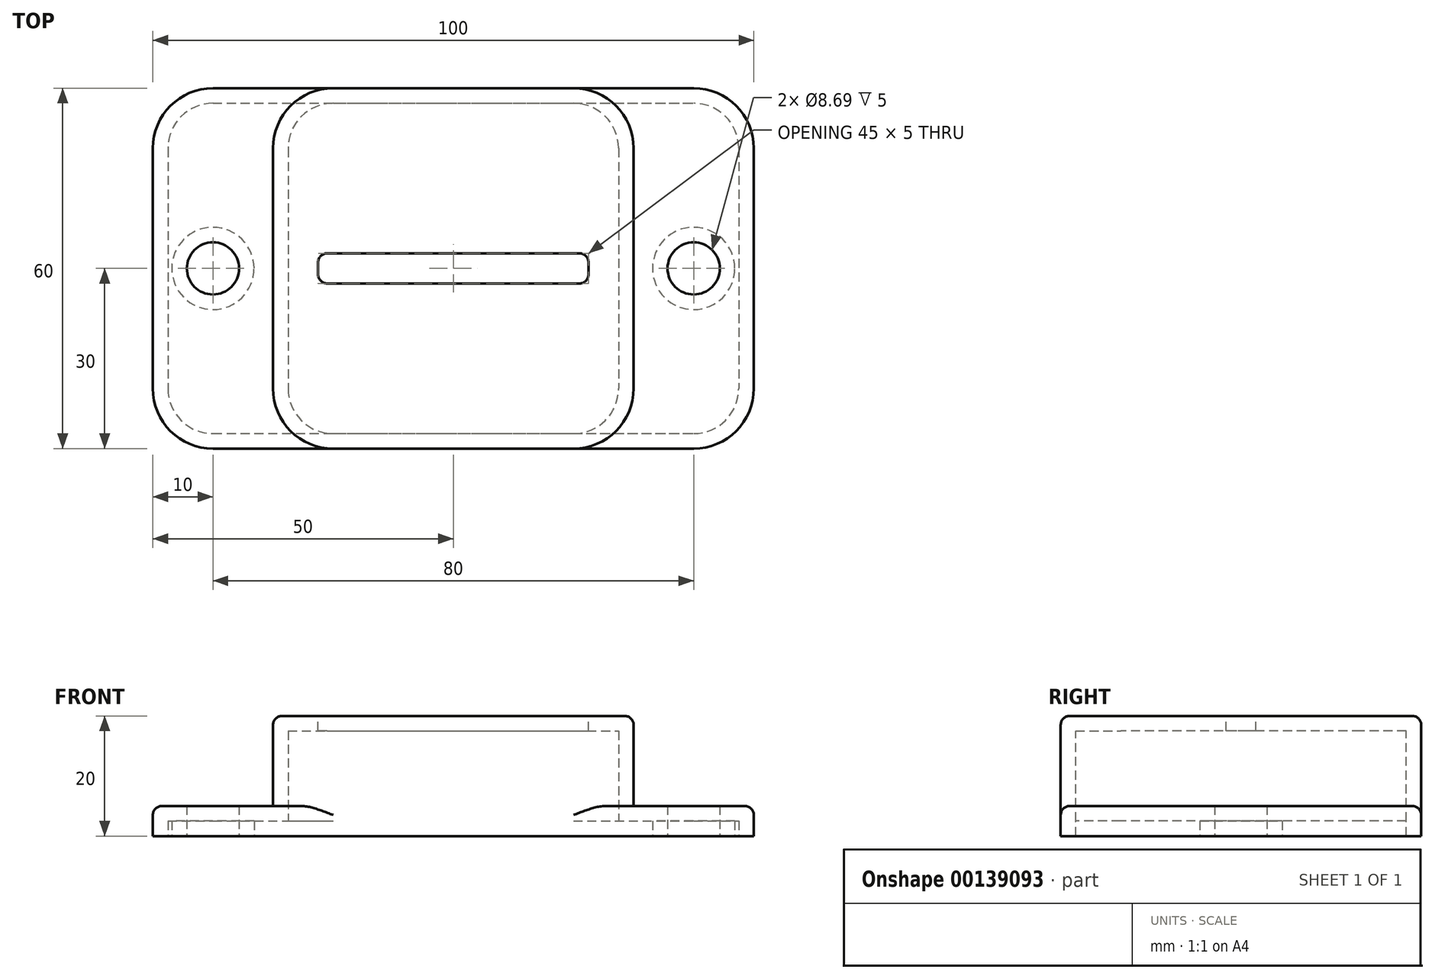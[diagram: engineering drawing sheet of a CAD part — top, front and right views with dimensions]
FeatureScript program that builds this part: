
annotation { "Feature Type Name" : "Feature", "Feature Type Description" : "" }
export const myFeature = defineFeature(function(context is Context, id is Id, definition is map)
    precondition{}
    {
        {
            var Q0;
            Q0=qCreatedBy(makeId("Top.planeOp"),FACE);
            var sketch = newSketch(context, id + "F0", { "sketchPlane" : qUnion([Q0])});
            skLineSegment(sketch, "E0.bottom", {"start": v(-40, 30) * mm, "end": v(40, 30) * mm});
            skLineSegment(sketch, "E0.top", {"start": v(-40, -30) * mm, "end": v(40, -30) * mm});
            skLineSegment(sketch, "E0.left", {"start": v(-50, 20) * mm, "end": v(-50, -20) * mm});
            skLineSegment(sketch, "E0.right", {"start": v(50, 20) * mm, "end": v(50, -20) * mm});
            skPoint(sketch, "E1.visualSharp", {"position": v(-50, -30) * mm});
            skArc(sketch, "E1.filletArc", {"start": v(-50, -20) * mm, "mid": v(-47.07, -27.07) * mm, "end": v(-40, -30) * mm});
            skPoint(sketch, "E2.visualSharp", {"position": v(-50, 30) * mm});
            skArc(sketch, "E2.filletArc", {"start": v(-40, 30) * mm, "mid": v(-47.07, 27.07) * mm, "end": v(-50, 20) * mm});
            skPoint(sketch, "E3.visualSharp", {"position": v(50, 30) * mm});
            skArc(sketch, "E3.filletArc", {"start": v(50, 20) * mm, "mid": v(47.07, 27.07) * mm, "end": v(40, 30) * mm});
            skPoint(sketch, "E4.visualSharp", {"position": v(50, -30) * mm});
            skArc(sketch, "E4.filletArc", {"start": v(40, -30) * mm, "mid": v(47.07, -27.07) * mm, "end": v(50, -20) * mm});
            skCircle(sketch, "E5", {"center": v(-40, 0) * mm, "radius": 4.34 * mm});
            skCircle(sketch, "E6", {"center": v(40, 0) * mm, "radius": 4.34 * mm});
            skSolve(sketch);
        }
        {
            var Q0;
            Q0=makeQuery(id+"F0.imprint","IMPRINT",FACE,{"disambiguationData":[TD([[makeQuery(id+"F0.imprint","IMPRINT",EDGE,{"derivedFrom":sQuery(id+"F0.wireOp",EDGE,"E0.bottom")}),-1.0]])]});
            extrude(context, id + "F1", {"entities" : qUnion([Q0]), "depth" : 5 * mm});
        }
        {
            var Q0;
            Q0=makeQuery(id+"F1.opExtrude","CAP_FACE",FACE,{"disambiguationData":[OSD([sQuery(id+"F0.wireOp",EDGE,"E0.bottom"),sQuery(id+"F0.wireOp",EDGE,"E0.top"),sQuery(id+"F0.wireOp",EDGE,"E0.left"),sQuery(id+"F0.wireOp",EDGE,"E0.right"),sQuery(id+"F0.wireOp",EDGE,"E1.filletArc"),sQuery(id+"F0.wireOp",EDGE,"E2.filletArc"),sQuery(id+"F0.wireOp",EDGE,"E3.filletArc"),sQuery(id+"F0.wireOp",EDGE,"E4.filletArc"),sQuery(id+"F0.wireOp",EDGE,"E5"),sQuery(id+"F0.wireOp",EDGE,"E6")])],"isStart":false});
            var sketch = newSketch(context, id + "F2", { "sketchPlane" : qUnion([Q0])});
            skLineSegment(sketch, "E7.bottom", {"start": v(-20, 30) * mm, "end": v(20, 30) * mm});
            skLineSegment(sketch, "E7.top", {"start": v(-20, -30) * mm, "end": v(20, -30) * mm});
            skLineSegment(sketch, "E7.left", {"start": v(-30, 20) * mm, "end": v(-30, -20) * mm});
            skLineSegment(sketch, "E7.right", {"start": v(30, 20) * mm, "end": v(30, -20) * mm});
            skPoint(sketch, "E8.visualSharp", {"position": v(-30, 30) * mm});
            skArc(sketch, "E8.filletArc", {"start": v(-20, 30) * mm, "mid": v(-27.07, 27.07) * mm, "end": v(-30, 20) * mm});
            skPoint(sketch, "E9.visualSharp", {"position": v(30, 30) * mm});
            skArc(sketch, "E9.filletArc", {"start": v(30, 20) * mm, "mid": v(27.07, 27.07) * mm, "end": v(20, 30) * mm});
            skPoint(sketch, "E10.visualSharp", {"position": v(30, -30) * mm});
            skArc(sketch, "E10.filletArc", {"start": v(20, -30) * mm, "mid": v(27.07, -27.07) * mm, "end": v(30, -20) * mm});
            skPoint(sketch, "E11.visualSharp", {"position": v(-30, -30) * mm});
            skArc(sketch, "E11.filletArc", {"start": v(-30, -20) * mm, "mid": v(-27.07, -27.07) * mm, "end": v(-20, -30) * mm});
            skSolve(sketch);
        }
        {
            var Q0;
            Q0=makeQuery(id+"F2.imprint","IMPRINT",FACE,{"disambiguationData":[TD([[makeQuery(id+"F2.imprint","IMPRINT",EDGE,{"derivedFrom":sQuery(id+"F2.wireOp",EDGE,"E7.bottom")}),-1.0]])]});
            extrude(context, id + "F3", {"entities" : qUnion([Q0]), "operationType" : NewBodyOperationType.ADD, "depth" : 15 * mm});
        }
        {
            var Q0;
            Q0=makeQuery(id+"F1.opExtrude","CAP_FACE",FACE,{"disambiguationData":[OSD([sQuery(id+"F0.wireOp",EDGE,"E0.bottom"),sQuery(id+"F0.wireOp",EDGE,"E0.top"),sQuery(id+"F0.wireOp",EDGE,"E0.left"),sQuery(id+"F0.wireOp",EDGE,"E0.right"),sQuery(id+"F0.wireOp",EDGE,"E1.filletArc"),sQuery(id+"F0.wireOp",EDGE,"E2.filletArc"),sQuery(id+"F0.wireOp",EDGE,"E3.filletArc"),sQuery(id+"F0.wireOp",EDGE,"E4.filletArc"),sQuery(id+"F0.wireOp",EDGE,"E5"),sQuery(id+"F0.wireOp",EDGE,"E6")])],"isStart":true});
            shell(context, id + "F4", {"entities" : qUnion([Q0]), "thickness" : 2.5 * mm});
        }
        {
            var Q0;
            Q0=makeQuery(id+"F3.opExtrude","CAP_FACE",FACE,{"disambiguationData":[OSD([sQuery(id+"F2.wireOp",EDGE,"E7.bottom"),sQuery(id+"F2.wireOp",EDGE,"E7.top"),sQuery(id+"F2.wireOp",EDGE,"E7.left"),sQuery(id+"F2.wireOp",EDGE,"E7.right"),sQuery(id+"F2.wireOp",EDGE,"E8.filletArc"),sQuery(id+"F2.wireOp",EDGE,"E9.filletArc"),sQuery(id+"F2.wireOp",EDGE,"E10.filletArc"),sQuery(id+"F2.wireOp",EDGE,"E11.filletArc")])],"isStart":false});
            var sketch = newSketch(context, id + "F5", { "sketchPlane" : qUnion([Q0])});
            skLineSegment(sketch, "E12.bottom", {"start": v(-22.5, 2.5) * mm, "end": v(22.5, 2.5) * mm});
            skLineSegment(sketch, "E12.top", {"start": v(-22.5, -2.5) * mm, "end": v(22.5, -2.5) * mm});
            skLineSegment(sketch, "E12.left", {"start": v(-22.5, 2.5) * mm, "end": v(-22.5, -2.5) * mm});
            skLineSegment(sketch, "E12.right", {"start": v(22.5, 2.5) * mm, "end": v(22.5, -2.5) * mm});
            skPoint(sketch, "E12.middle", {"position": v(0, 0) * mm});
            skSolve(sketch);
        }
        {
            var Q0;
            Q0=makeQuery(id+"F5.imprint","IMPRINT",FACE,{"disambiguationData":[TD([[makeQuery(id+"F5.imprint","IMPRINT",EDGE,{"derivedFrom":sQuery(id+"F5.wireOp",EDGE,"E12.bottom")}),-1.0]])]});
            extrude(context, id + "F6", {"entities" : qUnion([Q0]), "operationType" : NewBodyOperationType.REMOVE, "endBound" : BoundingType.THROUGH_ALL, "oppositeDirection" : true, "depth" : 25 * mm});
        }
        {
            var Q0;
            Q0=makeQuery(id+"F6.boolean.opBoolean","COPY",EDGE,{"derivedFrom":makeQuery(id+"F6.opExtrude","SWEPT_EDGE",EDGE,{"disambiguationData":[OSD([sQuery(id+"F5.wireOp",EDGE,"E12.bottom"),sQuery(id+"F5.wireOp",EDGE,"E12.left")])]})});
            var Q1;
            Q1=makeQuery(id+"F6.boolean.opBoolean","COPY",EDGE,{"derivedFrom":makeQuery(id+"F6.opExtrude","SWEPT_EDGE",EDGE,{"disambiguationData":[OSD([sQuery(id+"F5.wireOp",EDGE,"E12.top"),sQuery(id+"F5.wireOp",EDGE,"E12.left")])]})});
            var Q2;
            Q2=makeQuery(id+"F6.boolean.opBoolean","COPY",EDGE,{"derivedFrom":makeQuery(id+"F6.opExtrude","SWEPT_EDGE",EDGE,{"disambiguationData":[OSD([sQuery(id+"F5.wireOp",EDGE,"E12.bottom"),sQuery(id+"F5.wireOp",EDGE,"E12.right")])]})});
            var Q3;
            Q3=makeQuery(id+"F6.boolean.opBoolean","COPY",EDGE,{"derivedFrom":makeQuery(id+"F6.opExtrude","SWEPT_EDGE",EDGE,{"disambiguationData":[OSD([sQuery(id+"F5.wireOp",EDGE,"E12.top"),sQuery(id+"F5.wireOp",EDGE,"E12.right")])]})});
            var Q4;
            Q4=makeQuery(id+"F3.opExtrude","CAP_EDGE",EDGE,{"disambiguationData":[OSD([sQuery(id+"F2.wireOp",EDGE,"E7.right")])],"isStart":false});
            var Q5;
            Q5=makeQuery(id+"F3.opExtrude","CAP_EDGE",EDGE,{"disambiguationData":[OSD([sQuery(id+"F2.wireOp",EDGE,"E10.filletArc")])],"isStart":false});
            var Q6;
            Q6=makeQuery(id+"F3.opExtrude","CAP_EDGE",EDGE,{"disambiguationData":[OSD([sQuery(id+"F2.wireOp",EDGE,"E7.top")])],"isStart":false});
            var Q7;
            Q7=makeQuery(id+"F1.opExtrude","CAP_EDGE",EDGE,{"disambiguationData":[OSD([sQuery(id+"F0.wireOp",EDGE,"E3.filletArc")])],"isStart":false});
            var Q8;
            {var subQ0=sQuery(id+"F0.wireOp",EDGE,"E1.filletArc");var subQ1=sQuery(id+"F0.wireOp",EDGE,"E0.top");Q8=makeQuery(id+"F3.boolean.opBoolean","SPLIT",EDGE,{"disambiguationData":[TD([makeQuery(id+"F1.opExtrude","SWEPT_FACE",FACE,{"disambiguationData":[OSD([subQ0])]})])],"derivedFrom":makeQuery(id+"F1.opExtrude","CAP_EDGE",EDGE,{"disambiguationData":[OSD([subQ1])],"isStart":false})});}
            fillet(context, id + "F7", {"entities" : qUnion([Q0, Q1, Q2, Q3, Q4, Q5, Q6, Q7, Q8]), "radius" : 1.5 * mm, "tangentPropagation" : true, "allowEdgeOverflow" : false});
        }
    });
